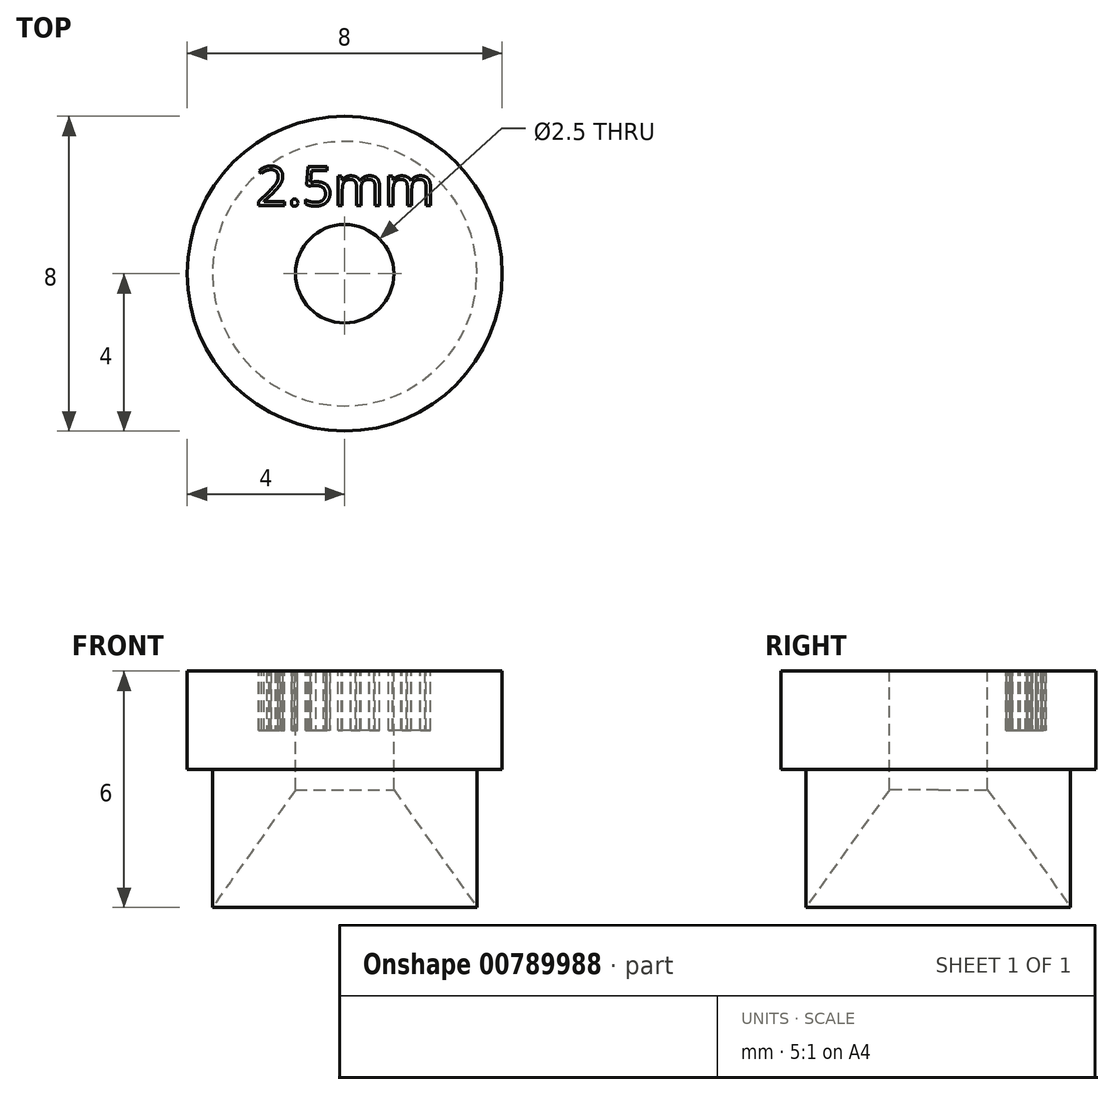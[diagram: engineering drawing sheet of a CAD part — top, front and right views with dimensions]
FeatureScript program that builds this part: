
annotation { "Feature Type Name" : "Feature", "Feature Type Description" : "" }
export const myFeature = defineFeature(function(context is Context, id is Id, definition is map)
    precondition{}
    {
        {
            var Q0;
            Q0=qCreatedBy(makeId("Front.planeOp"),FACE);
            var sketch = newSketch(context, id + "F0", { "sketchPlane" : qUnion([Q0])});
            skLineSegment(sketch, "E0", {"start": v(0, 0) * mm, "end": v(-4, 0) * mm});
            skLineSegment(sketch, "E1", {"start": v(-4, 0) * mm, "end": v(-4, -2.5) * mm});
            skLineSegment(sketch, "E2", {"start": v(-4, -2.5) * mm, "end": v(-3.36, -2.5) * mm});
            skLineSegment(sketch, "E3", {"start": v(-3.36, -2.5) * mm, "end": v(-3.36, -6) * mm});
            skLineSegment(sketch, "E4", {"start": v(-3.36, -6) * mm, "end": v(0, -1.25) * mm});
            skLineSegment(sketch, "E5", {"start": v(0, -1.25) * mm, "end": v(0, 0) * mm});
            skPoint(sketch, "E6", {"position": v(-4, -1.25) * mm});
            skSolve(sketch);
        }
        {
            var Q0;
            Q0=makeQuery(id+"F0.imprint","IMPRINT",FACE,{"disambiguationData":[TD([[makeQuery(id+"F0.imprint","IMPRINT",EDGE,{"derivedFrom":sQuery(id+"F0.wireOp",EDGE,"E0")}),1.0]])]});
            var Q1;
            Q1=sQuery(id+"F0.wireOp",EDGE,"E5");
            revolve(context, id + "F1", {"surfaceOperationType" : NewSurfaceOperationType.NEW, "entities" : qUnion([Q0]), "axis" : qUnion([Q1]), "revolveType" : RevolveType.FULL});
        }
        {
            var Q0;
            Q0=makeQuery(id+"F1.opRevolve","SWEPT_FACE",FACE,{"disambiguationData":[OSD([sQuery(id+"F0.wireOp",EDGE,"E0")])]});
            var sketch = newSketch(context, id + "F2", { "sketchPlane" : qUnion([Q0])});
            skText(sketch, "E7", { "text": "2.5mm", "fontName": "OpenSans-Regular.ttf"});
            skCircle(sketch, "E8", {"center": v(0, 0) * mm, "radius": 1.25 * mm});
            const initialGuessF2  = {"E7": [-0.00225, 0.00173, 1, 0, 0.001]};
            skSetInitialGuess(sketch, initialGuessF2);
            skSolve(sketch);
        }
        {
            var Q0;
            Q0=makeQuery(id+"F2.imprint","IMPRINT",FACE,{"disambiguationData":[TD([[makeQuery(id+"F2.imprint","IMPRINT",EDGE,{"derivedFrom":sQuery(id+"F2.wireOp",EDGE,"2dIevTCF-Ez6s-lGD7-yDb0-U2i28K1mrw8J")}),1.0]])]});
            var Q1;
            Q1=makeQuery(id+"F2.imprint","IMPRINT",FACE,{"disambiguationData":[TD([[makeQuery(id+"F2.imprint","IMPRINT",EDGE,{"derivedFrom":sQuery(id+"F2.wireOp",EDGE,"rJ3fZz3p-6w1M-4B26-fppL-qMqxoA7VBc3G")}),1.0]])]});
            var Q2;
            Q2=makeQuery(id+"F2.imprint","IMPRINT",FACE,{"disambiguationData":[TD([[makeQuery(id+"F2.imprint","IMPRINT",EDGE,{"derivedFrom":sQuery(id+"F2.wireOp",EDGE,"E8")}),1.0]])]});
            extrude(context, id + "F3", {"entities" : qUnion([Q0, Q1, Q2]), "operationType" : NewBodyOperationType.REMOVE, "oppositeDirection" : true, "depth" : 25 * mm, "offsetDistance" : 25 * mm});
        }
        {
            var Q0;
            Q0 = qSketchRegion(id + "F2", true);
            extrude(context, id + "F4", {"entities" : qUnion([Q0]), "operationType" : NewBodyOperationType.REMOVE, "oppositeDirection" : true, "depth" : 1.5 * mm, "offsetDistance" : 25 * mm});
        }
    });
